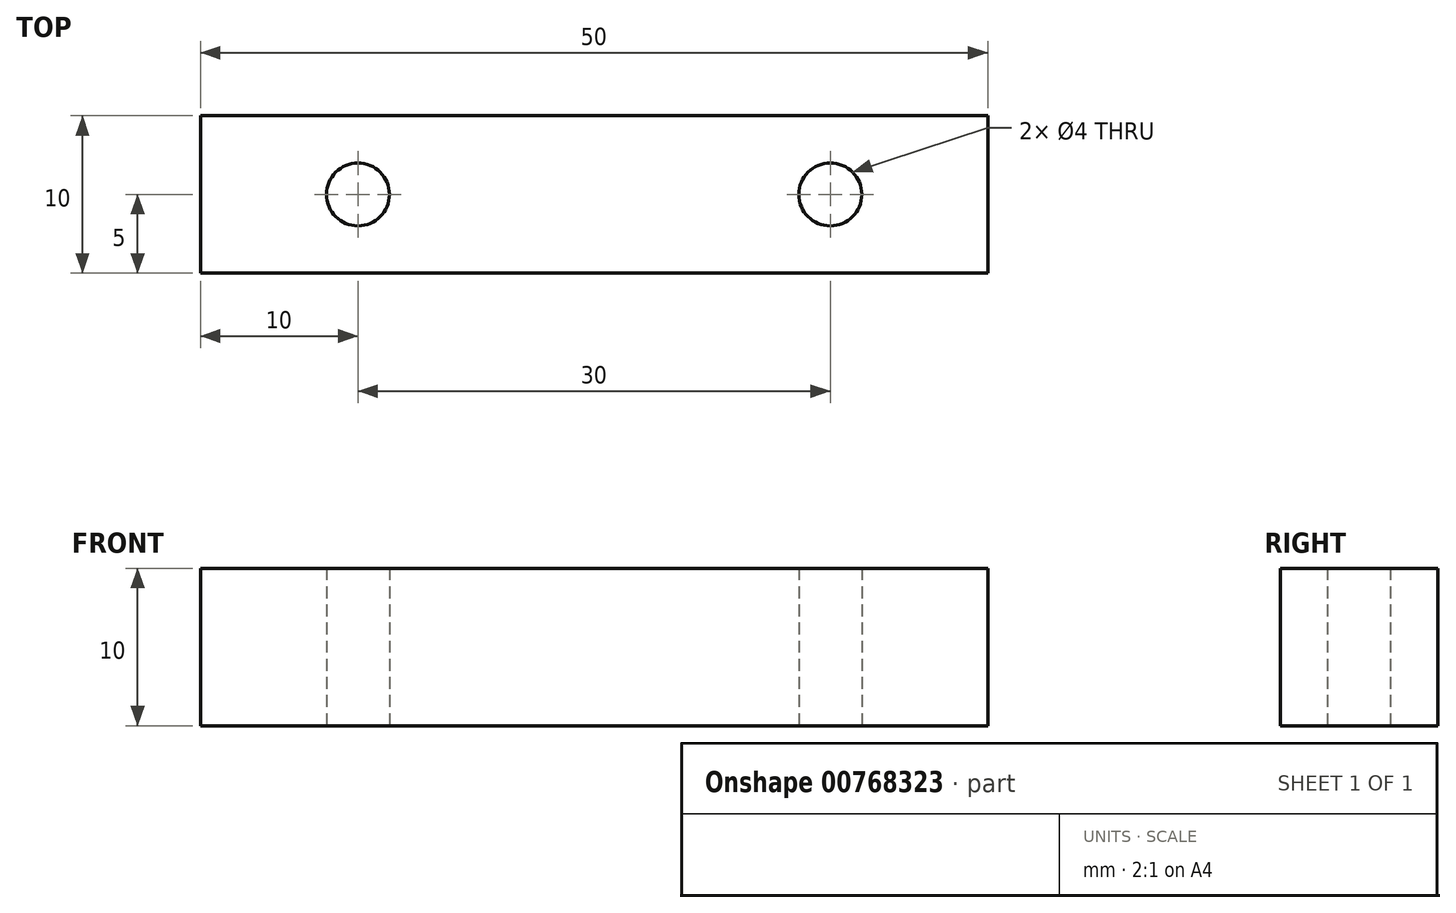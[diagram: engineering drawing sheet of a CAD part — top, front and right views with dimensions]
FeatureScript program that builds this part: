
annotation { "Feature Type Name" : "Feature", "Feature Type Description" : "" }
export const myFeature = defineFeature(function(context is Context, id is Id, definition is map)
    precondition{}
    {
        {
            var Q0;
            Q0=qCreatedBy(makeId("Top.planeOp"),FACE);
            var sketch = newSketch(context, id + "F0", { "sketchPlane" : qUnion([Q0])});
            skLineSegment(sketch, "E0.bottom", {"start": v(25, -5) * mm, "end": v(-25, -5) * mm});
            skLineSegment(sketch, "E0.top", {"start": v(25, 5) * mm, "end": v(-25, 5) * mm});
            skLineSegment(sketch, "E0.left", {"start": v(25, -5) * mm, "end": v(25, 5) * mm});
            skLineSegment(sketch, "E0.right", {"start": v(-25, -5) * mm, "end": v(-25, 5) * mm});
            skPoint(sketch, "E0.middle", {"position": v(0, 0) * mm});
            skCircle(sketch, "E1", {"center": v(-15, 0) * mm, "radius": 2 * mm});
            skCircle(sketch, "E2", {"center": v(15, 0) * mm, "radius": 2 * mm});
            skSolve(sketch);
        }
        {
            var Q0;
            Q0 = qSketchRegion(id + "F0", true);
            extrude(context, id + "F1", {"entities" : qUnion([Q0]), "depth" : 10 * mm, "offsetDistance" : 25 * mm});
        }
    });
